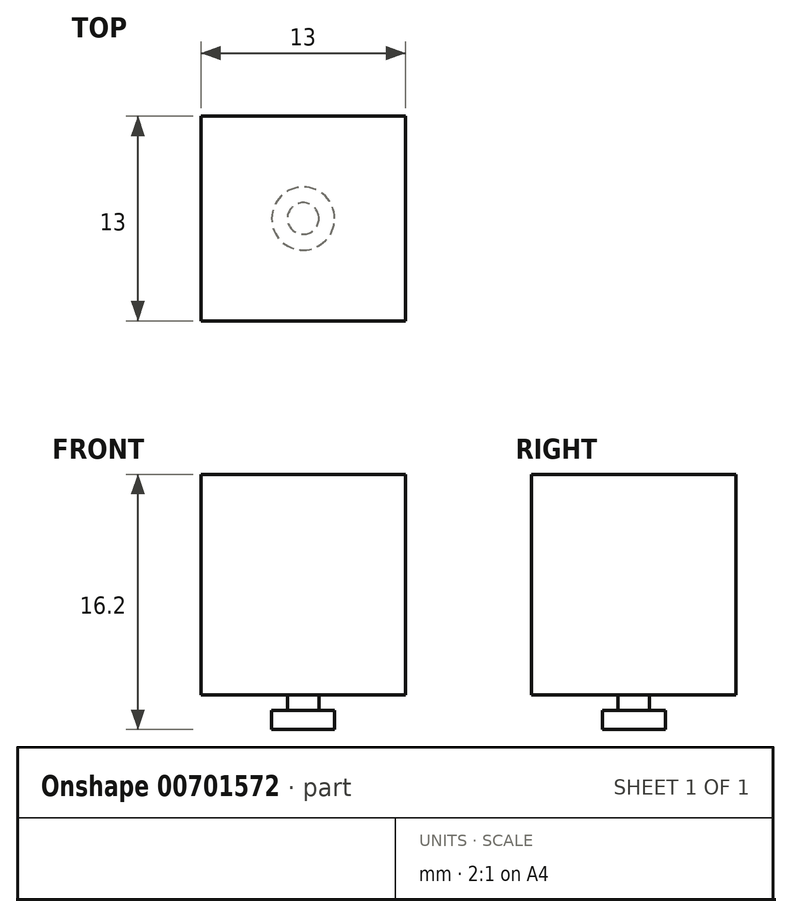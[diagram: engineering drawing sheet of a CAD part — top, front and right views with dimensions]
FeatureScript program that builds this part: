
annotation { "Feature Type Name" : "Feature", "Feature Type Description" : "" }
export const myFeature = defineFeature(function(context is Context, id is Id, definition is map)
    precondition{}
    {
        {
            var Q0;
            Q0=qCreatedBy(makeId("Top.planeOp"),FACE);
            var sketch = newSketch(context, id + "F0", { "sketchPlane" : qUnion([Q0])});
            skLineSegment(sketch, "E0.bottom", {"start": v(6.5, 6.5) * mm, "end": v(-6.5, 6.5) * mm});
            skLineSegment(sketch, "E0.top", {"start": v(6.5, -6.5) * mm, "end": v(-6.5, -6.5) * mm});
            skLineSegment(sketch, "E0.left", {"start": v(6.5, 6.5) * mm, "end": v(6.5, -6.5) * mm});
            skLineSegment(sketch, "E0.right", {"start": v(-6.5, 6.5) * mm, "end": v(-6.5, -6.5) * mm});
            skPoint(sketch, "E0.middle", {"position": v(0, 0) * mm});
            skSolve(sketch);
        }
        {
            var Q0;
            Q0 = qSketchRegion(id + "F0", true);
            extrude(context, id + "F1", {"entities" : qUnion([Q0]), "depth" : 14 * mm, "offsetDistance" : 25 * mm});
        }
        {
            var Q0;
            Q0=makeQuery(id+"F1.opExtrude","CAP_FACE",FACE,{"disambiguationData":[OSD([sQuery(id+"F0.wireOp",EDGE,"E0.bottom"),sQuery(id+"F0.wireOp",EDGE,"E0.top"),sQuery(id+"F0.wireOp",EDGE,"E0.left"),sQuery(id+"F0.wireOp",EDGE,"E0.right")])],"isStart":true});
            var sketch = newSketch(context, id + "F2", { "sketchPlane" : qUnion([Q0])});
            skCircle(sketch, "E1", {"center": v(0, 0) * mm, "radius": 1 * mm});
            skSolve(sketch);
        }
        {
            var Q0;
            Q0 = qSketchRegion(id + "F2", true);
            extrude(context, id + "F3", {"entities" : qUnion([Q0]), "operationType" : NewBodyOperationType.ADD, "depth" : 1 * mm, "offsetDistance" : 25 * mm});
        }
        {
            var Q0;
            Q0=makeQuery(id+"F3.opExtrude","CAP_FACE",FACE,{"disambiguationData":[OSD([sQuery(id+"F2.wireOp",EDGE,"E1")])],"isStart":false});
            var sketch = newSketch(context, id + "F4", { "sketchPlane" : qUnion([Q0])});
            skCircle(sketch, "E2", {"center": v(0, 0) * mm, "radius": 2 * mm});
            skSolve(sketch);
        }
        {
            var Q0;
            Q0 = qSketchRegion(id + "F4", true);
            extrude(context, id + "F5", {"entities" : qUnion([Q0]), "operationType" : NewBodyOperationType.ADD, "depth" : 1.2 * mm, "offsetDistance" : 25 * mm});
        }
    });
